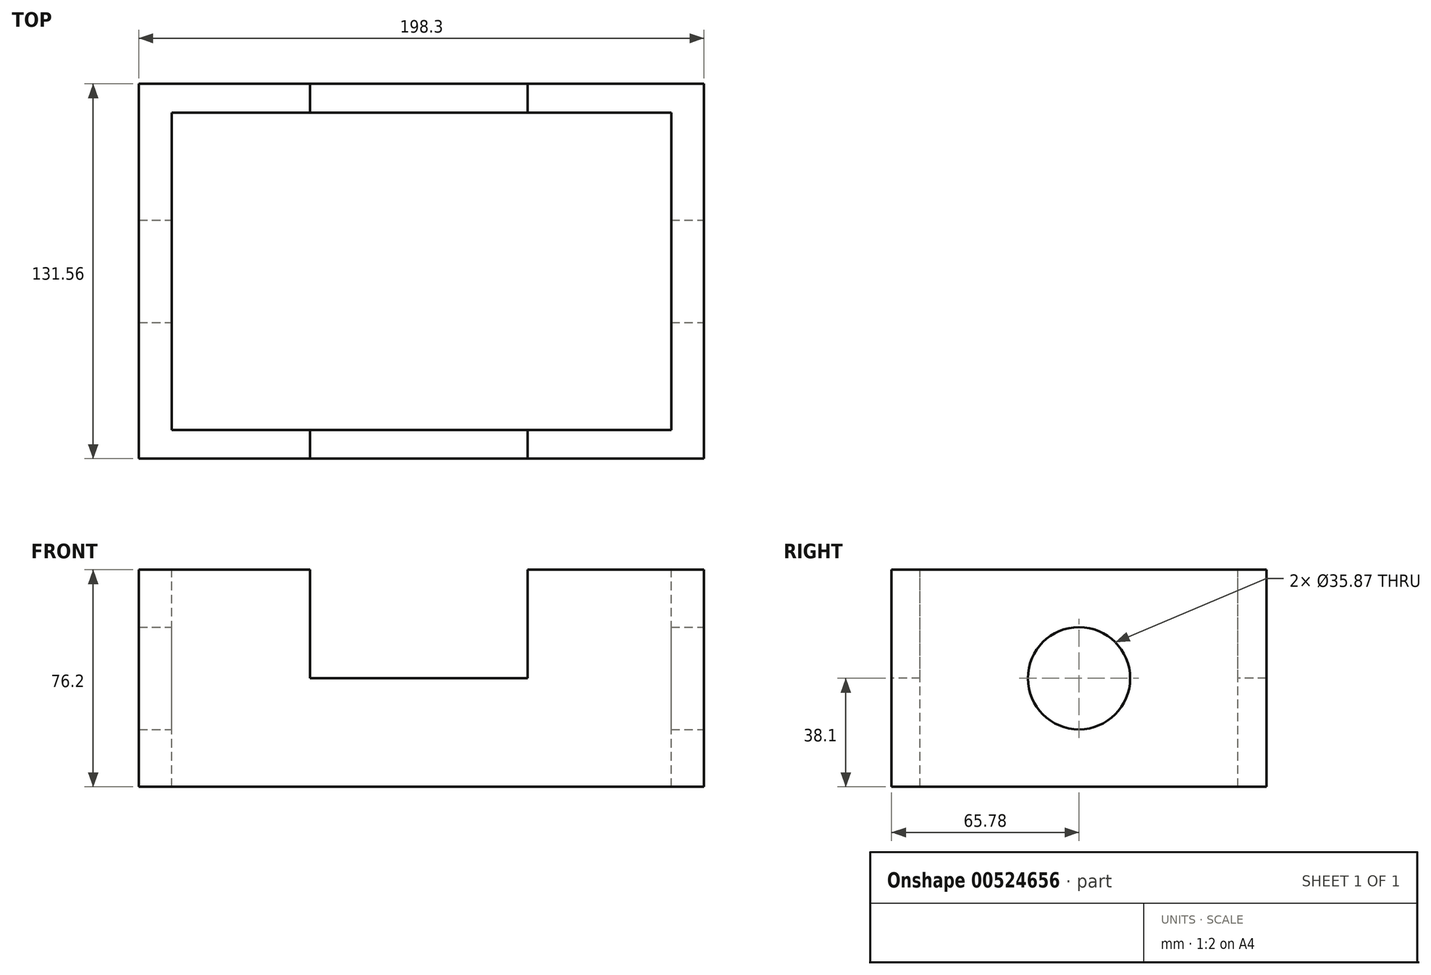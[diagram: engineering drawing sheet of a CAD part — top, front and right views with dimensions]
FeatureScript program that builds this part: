
annotation { "Feature Type Name" : "Feature", "Feature Type Description" : "" }
export const myFeature = defineFeature(function(context is Context, id is Id, definition is map)
    precondition{}
    {
        {
            var Q0;
            Q0=qCreatedBy(makeId("Top.planeOp"),FACE);
            var sketch = newSketch(context, id + "F0", { "sketchPlane" : qUnion([Q0])});
            skLineSegment(sketch, "E0.bottom", {"start": v(99.15, -65.78) * mm, "end": v(-99.15, -65.78) * mm});
            skLineSegment(sketch, "E0.top", {"start": v(99.15, 65.78) * mm, "end": v(-99.15, 65.78) * mm});
            skLineSegment(sketch, "E0.left", {"start": v(99.15, -65.78) * mm, "end": v(99.15, 65.78) * mm});
            skLineSegment(sketch, "E0.right", {"start": v(-99.15, -65.78) * mm, "end": v(-99.15, 65.78) * mm});
            skPoint(sketch, "E0.middle", {"position": v(0, 0) * mm});
            skSolve(sketch);
        }
        {
            var Q0;
            Q0=makeQuery(id+"F0.imprint","IMPRINT",FACE,{"disambiguationData":[TD([[makeQuery(id+"F0.imprint","IMPRINT",EDGE,{"derivedFrom":sQuery(id+"F0.wireOp",EDGE,"E0.bottom")}),-1.0]])]});
            extrude(context, id + "F1", {"entities" : qUnion([Q0]), "depth" : 76.2 * mm, "offsetDistance" : 25.4 * mm});
        }
        {
            var Q0;
            Q0=makeQuery(id+"F1.opExtrude","CAP_FACE",FACE,{"disambiguationData":[OSD([sQuery(id+"F0.wireOp",EDGE,"E0.bottom"),sQuery(id+"F0.wireOp",EDGE,"E0.top"),sQuery(id+"F0.wireOp",EDGE,"E0.left"),sQuery(id+"F0.wireOp",EDGE,"E0.right")])],"isStart":false});
            var sketch = newSketch(context, id + "F2", { "sketchPlane" : qUnion([Q0])});
            skLineSegment(sketch, "E1.bottom", {"start": v(87.62, -55.71) * mm, "end": v(-87.62, -55.71) * mm});
            skLineSegment(sketch, "E1.top", {"start": v(87.62, 55.71) * mm, "end": v(-87.62, 55.71) * mm});
            skLineSegment(sketch, "E1.left", {"start": v(87.62, -55.71) * mm, "end": v(87.62, 55.71) * mm});
            skLineSegment(sketch, "E1.right", {"start": v(-87.62, -55.71) * mm, "end": v(-87.62, 55.71) * mm});
            skPoint(sketch, "E1.middle", {"position": v(0, 0) * mm});
            skSolve(sketch);
        }
        {
            var Q0;
            Q0=makeQuery(id+"F2.imprint","IMPRINT",FACE,{"disambiguationData":[TD([[makeQuery(id+"F2.imprint","IMPRINT",EDGE,{"derivedFrom":sQuery(id+"F2.wireOp",EDGE,"E1.bottom")}),-1.0]])]});
            extrude(context, id + "F3", {"entities" : qUnion([Q0]), "operationType" : NewBodyOperationType.REMOVE, "endBound" : BoundingType.THROUGH_ALL, "oppositeDirection" : true, "depth" : 25.4 * mm, "offsetDistance" : 25.4 * mm});
        }
        {
            var Q0;
            Q0=makeQuery(id+"F1.opExtrude","SWEPT_FACE",FACE,{"disambiguationData":[OSD([sQuery(id+"F0.wireOp",EDGE,"E0.left")])]});
            var sketch = newSketch(context, id + "F4", { "sketchPlane" : qUnion([Q0])});
            skCircle(sketch, "E2", {"center": v(0, 38.1) * mm, "radius": 17.94 * mm});
            skPoint(sketch, "E2.centerSnap0", {"position": v(-65.78, 38.1) * mm});
            skSolve(sketch);
        }
        {
            var Q0;
            Q0=makeQuery(id+"F4.imprint","IMPRINT",FACE,{"disambiguationData":[TD([[makeQuery(id+"F4.imprint","IMPRINT",EDGE,{"derivedFrom":sQuery(id+"F4.wireOp",EDGE,"E2")}),1.0]])]});
            extrude(context, id + "F5", {"entities" : qUnion([Q0]), "operationType" : NewBodyOperationType.REMOVE, "endBound" : BoundingType.THROUGH_ALL, "oppositeDirection" : true, "depth" : 25.4 * mm, "offsetDistance" : 25.4 * mm});
        }
        {
            var Q0;
            Q0=makeQuery(id+"F1.opExtrude","CAP_FACE",FACE,{"disambiguationData":[OSD([sQuery(id+"F0.wireOp",EDGE,"E0.bottom"),sQuery(id+"F0.wireOp",EDGE,"E0.top"),sQuery(id+"F0.wireOp",EDGE,"E0.left"),sQuery(id+"F0.wireOp",EDGE,"E0.right")])],"isStart":false});
            var sketch = newSketch(context, id + "F6", { "sketchPlane" : qUnion([Q0])});
            skLineSegment(sketch, "E3.bottom", {"start": v(-39.02, 65.78) * mm, "end": v(37.3, 65.78) * mm});
            skLineSegment(sketch, "E3.top", {"start": v(-39.02, 55.71) * mm, "end": v(37.3, 55.71) * mm});
            skLineSegment(sketch, "E3.left", {"start": v(-39.02, 65.78) * mm, "end": v(-39.02, 55.71) * mm});
            skLineSegment(sketch, "E3.right", {"start": v(37.3, 65.78) * mm, "end": v(37.3, 55.71) * mm});
            skLineSegment(sketch, "E4.bottom", {"start": v(-39.02, -55.71) * mm, "end": v(37.3, -55.71) * mm});
            skLineSegment(sketch, "E4.top", {"start": v(-39.02, -65.78) * mm, "end": v(37.3, -65.78) * mm});
            skLineSegment(sketch, "E4.left", {"start": v(-39.02, -55.71) * mm, "end": v(-39.02, -65.78) * mm});
            skLineSegment(sketch, "E4.right", {"start": v(37.3, -55.71) * mm, "end": v(37.3, -65.78) * mm});
            skSolve(sketch);
        }
        {
            var Q0;
            Q0=makeQuery(id+"F6.imprint","IMPRINT",FACE,{"disambiguationData":[TD([[makeQuery(id+"F6.imprint","IMPRINT",EDGE,{"derivedFrom":sQuery(id+"F6.wireOp",EDGE,"E3.bottom")}),1.0]])]});
            var Q1;
            Q1=makeQuery(id+"F6.imprint","IMPRINT",FACE,{"disambiguationData":[TD([[makeQuery(id+"F6.imprint","IMPRINT",EDGE,{"derivedFrom":sQuery(id+"F6.wireOp",EDGE,"E4.bottom")}),1.0]])]});
            extrude(context, id + "F7", {"entities" : qUnion([Q0, Q1]), "operationType" : NewBodyOperationType.REMOVE, "oppositeDirection" : true, "depth" : 38.1 * mm, "offsetDistance" : 25.4 * mm});
        }
    });
